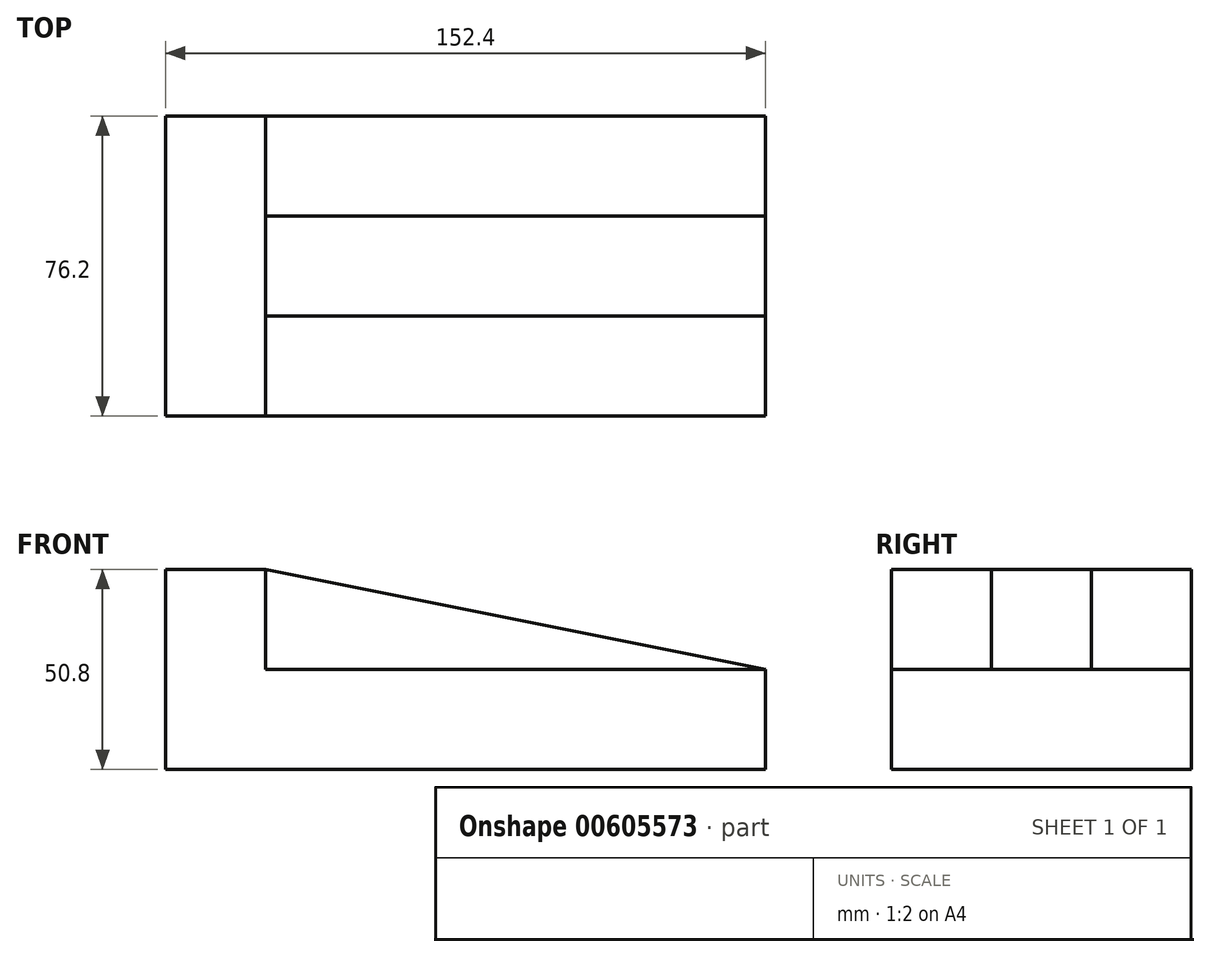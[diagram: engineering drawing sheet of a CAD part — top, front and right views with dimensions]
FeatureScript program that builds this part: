
annotation { "Feature Type Name" : "Feature", "Feature Type Description" : "" }
export const myFeature = defineFeature(function(context is Context, id is Id, definition is map)
    precondition{}
    {
        {
            var Q0;
            Q0=qCreatedBy(makeId("Front.planeOp"),FACE);
            var sketch = newSketch(context, id + "F0", { "sketchPlane" : qUnion([Q0])});
            skLineSegment(sketch, "E0", {"start": v(0, 0) * mm, "end": v(152.4, 0) * mm});
            skLineSegment(sketch, "E1", {"start": v(152.4, 0) * mm, "end": v(152.4, 25.4) * mm});
            skLineSegment(sketch, "E2", {"start": v(152.4, 25.4) * mm, "end": v(25.4, 25.4) * mm});
            skLineSegment(sketch, "E3", {"start": v(25.4, 25.4) * mm, "end": v(25.4, 50.8) * mm});
            skLineSegment(sketch, "E4", {"start": v(25.4, 50.8) * mm, "end": v(0, 50.8) * mm});
            skLineSegment(sketch, "E5", {"start": v(0, 50.8) * mm, "end": v(0, 0) * mm});
            skSolve(sketch);
        }
        {
            var Q0;
            Q0=makeQuery(id+"F0.imprint","IMPRINT",FACE,{"disambiguationData":[TD([[makeQuery(id+"F0.imprint","IMPRINT",EDGE,{"derivedFrom":sQuery(id+"F0.wireOp",EDGE,"E0")}),1.0]])]});
            extrude(context, id + "F1", {"entities" : qUnion([Q0]), "depth" : 76.2 * mm, "offsetDistance" : 25.4 * mm});
        }
        {
            var Q0;
            Q0=makeQuery(id+"F1.opExtrude","SWEPT_FACE",FACE,{"disambiguationData":[OSD([sQuery(id+"F0.wireOp",EDGE,"E2")])]});
            var sketch = newSketch(context, id + "F2", { "sketchPlane" : qUnion([Q0])});
            skLineSegment(sketch, "E6", {"start": v(25.4, -50.8) * mm, "end": v(152.4, -50.8) * mm});
            skLineSegment(sketch, "E7", {"start": v(152.4, -50.8) * mm, "end": v(152.4, -25.4) * mm});
            skLineSegment(sketch, "E8", {"start": v(152.4, -25.4) * mm, "end": v(25.4, -25.4) * mm});
            skLineSegment(sketch, "E9", {"start": v(25.4, -25.4) * mm, "end": v(25.4, -50.8) * mm});
            skSolve(sketch);
        }
        {
            var Q0;
            Q0=makeQuery(id+"F2.imprint","IMPRINT",FACE,{"disambiguationData":[TD([[makeQuery(id+"F2.imprint","IMPRINT",EDGE,{"derivedFrom":sQuery(id+"F2.wireOp",EDGE,"E6")}),1.0]])]});
            extrude(context, id + "F3", {"entities" : qUnion([Q0]), "operationType" : NewBodyOperationType.ADD, "depth" : 25.4 * mm, "offsetDistance" : 25.4 * mm});
        }
        {
            var Q0;
            Q0=makeQuery(id+"F3.opExtrude","SWEPT_FACE",FACE,{"disambiguationData":[OSD([sQuery(id+"F2.wireOp",EDGE,"E6")])]});
            var sketch = newSketch(context, id + "F4", { "sketchPlane" : qUnion([Q0])});
            skLineSegment(sketch, "E10", {"start": v(25.4, 50.8) * mm, "end": v(152.4, 25.4) * mm});
            skLineSegment(sketch, "E11", {"start": v(152.4, 25.4) * mm, "end": v(152.4, 50.8) * mm});
            skLineSegment(sketch, "E12", {"start": v(152.4, 50.8) * mm, "end": v(25.4, 50.8) * mm});
            skSolve(sketch);
        }
        {
            var Q0;
            Q0=makeQuery(id+"F4.imprint","IMPRINT",FACE,{"disambiguationData":[TD([[makeQuery(id+"F4.imprint","IMPRINT",EDGE,{"derivedFrom":sQuery(id+"F4.wireOp",EDGE,"E10")}),1.0]])]});
            extrude(context, id + "F5", {"entities" : qUnion([Q0]), "operationType" : NewBodyOperationType.REMOVE, "oppositeDirection" : true, "depth" : 25.4 * mm, "offsetDistance" : 25.4 * mm});
        }
    });
